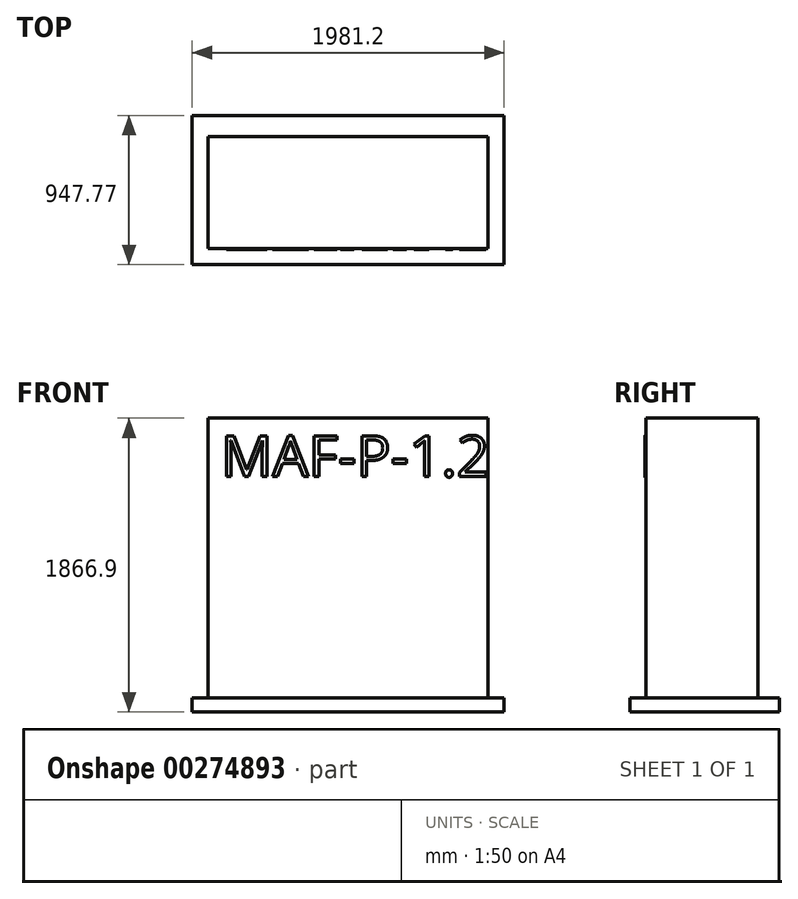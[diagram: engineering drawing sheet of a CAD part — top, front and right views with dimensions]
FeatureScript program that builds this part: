
annotation { "Feature Type Name" : "Feature", "Feature Type Description" : "" }
export const myFeature = defineFeature(function(context is Context, id is Id, definition is map)
    precondition{}
    {
        {
            var Q0;
            Q0=qCreatedBy(makeId("Top.planeOp"),FACE);
            var sketch = newSketch(context, id + "F0", { "sketchPlane" : qUnion([Q0])});
            skLineSegment(sketch, "E0.bottom", {"start": v(0, 0) * mm, "end": v(1778, 0) * mm});
            skLineSegment(sketch, "E0.top", {"start": v(0, 711.2) * mm, "end": v(1778, 711.2) * mm});
            skLineSegment(sketch, "E0.left", {"start": v(0, 0) * mm, "end": v(0, 711.2) * mm});
            skLineSegment(sketch, "E0.right", {"start": v(1778, 0) * mm, "end": v(1778, 711.2) * mm});
            skSolve(sketch);
        }
        {
            var Q0;
            Q0=makeQuery(id+"F0.imprint","IMPRINT",FACE,{"disambiguationData":[TD([[makeQuery(id+"F0.imprint","IMPRINT",EDGE,{"derivedFrom":sQuery(id+"F0.wireOp",EDGE,"E0.bottom")}),1.0]])]});
            extrude(context, id + "F1", {"entities" : qUnion([Q0]), "depth" : 1778 * mm});
        }
        {
            var Q0;
            Q0=makeQuery(id+"F1.opExtrude","SWEPT_FACE",FACE,{"disambiguationData":[OSD([sQuery(id+"F0.wireOp",EDGE,"E0.bottom")])]});
            var sketch = newSketch(context, id + "F2", { "sketchPlane" : qUnion([Q0])});
            skText(sketch, "E1", { "text": "MAF-P-1.2", "fontName": "OpenSans-Regular.ttf"});
            const initialGuessF2  = {"E1": [0.08221, 1.40756, 1, 0, 0.26045]};
            skSetInitialGuess(sketch, initialGuessF2);
            skSolve(sketch);
        }
        {
            var Q0;
            Q0 = qSketchRegion(id + "F2", true);
            extrude(context, id + "F3", {"entities" : qUnion([Q0]), "operationType" : NewBodyOperationType.ADD, "depth" : 6.35 * mm});
        }
        {
            var Q0;
            Q0=makeQuery(id+"F1.opExtrude","CAP_FACE",FACE,{"disambiguationData":[OSD([sQuery(id+"F0.wireOp",EDGE,"E0.bottom"),sQuery(id+"F0.wireOp",EDGE,"E0.top"),sQuery(id+"F0.wireOp",EDGE,"E0.left"),sQuery(id+"F0.wireOp",EDGE,"E0.right")])],"isStart":true});
            extrude(context, id + "F4", {"entities" : qUnion([Q0]), "operationType" : NewBodyOperationType.ADD, "depth" : 88.9 * mm});
        }
        {
            var Q0;
            {var subQ0=sQuery(id+"F0.wireOp",EDGE,"E0.left");Q0=makeQuery(id+"F4.boolean.opBoolean","MERGE",FACE,{"derivedFrom":[makeQuery(id+"F1.opExtrude","SWEPT_FACE",FACE,{"disambiguationData":[OSD([subQ0])]}),makeQuery(id+"F4.opExtrude","SWEPT_FACE",FACE,{"disambiguationData":[OSD([subQ0])]})]});}
            var sketch = newSketch(context, id + "F5", { "sketchPlane" : qUnion([Q0])});
            skLineSegment(sketch, "E2.bottom", {"start": v(-711.2, -88.9) * mm, "end": v(0, -88.9) * mm});
            skLineSegment(sketch, "E2.top", {"start": v(-711.2, 0) * mm, "end": v(0, 0) * mm});
            skLineSegment(sketch, "E2.left", {"start": v(-711.2, -88.9) * mm, "end": v(-711.2, 0) * mm});
            skLineSegment(sketch, "E2.right", {"start": v(0, -88.9) * mm, "end": v(0, 0) * mm});
            skSolve(sketch);
        }
        {
            var Q0;
            Q0=makeQuery(id+"F5.imprint","IMPRINT",FACE,{"disambiguationData":[TD([[makeQuery(id+"F5.imprint","IMPRINT",EDGE,{"derivedFrom":sQuery(id+"F5.wireOp",EDGE,"E2.bottom")}),-1.0]])]});
            extrude(context, id + "F6", {"entities" : qUnion([Q0]), "operationType" : NewBodyOperationType.ADD, "depth" : 101.6 * mm});
        }
        {
            var Q0;
            {var subQ0=sQuery(id+"F0.wireOp",EDGE,"E0.bottom");var subQ1=sQuery(id+"F0.wireOp",EDGE,"E0.left");Q0=makeQuery(id+"F6.boolean.opBoolean","MERGE",FACE,{"derivedFrom":[makeQuery(id+"F4.boolean.opBoolean","MERGE",FACE,{"derivedFrom":[makeQuery(id+"F3.boolean.opBoolean","SPLIT",FACE,{"disambiguationData":[TD([makeQuery(id+"F1.opExtrude","SWEPT_FACE",FACE,{"disambiguationData":[OSD([subQ1])]})])],"derivedFrom":makeQuery(id+"F1.opExtrude","SWEPT_FACE",FACE,{"disambiguationData":[OSD([subQ0])]})}),makeQuery(id+"F4.opExtrude","SWEPT_FACE",FACE,{"disambiguationData":[OSD([subQ0])]})]}),makeQuery(id+"F6.opExtrude","SWEPT_FACE",FACE,{"disambiguationData":[OSD([sQuery(id+"F5.wireOp",EDGE,"E2.right")])]})]});}
            var sketch = newSketch(context, id + "F7", { "sketchPlane" : qUnion([Q0])});
            skLineSegment(sketch, "E3.bottom", {"start": v(-101.6, -88.9) * mm, "end": v(1778, -88.9) * mm});
            skLineSegment(sketch, "E3.top", {"start": v(-101.6, 0) * mm, "end": v(1778, 0) * mm});
            skLineSegment(sketch, "E3.left", {"start": v(-101.6, -88.9) * mm, "end": v(-101.6, 0) * mm});
            skLineSegment(sketch, "E3.right", {"start": v(1778, -88.9) * mm, "end": v(1778, 0) * mm});
            skSolve(sketch);
        }
        {
            var Q0;
            Q0 = qSketchRegion(id + "F7", true);
            extrude(context, id + "F8", {"entities" : qUnion([Q0]), "operationType" : NewBodyOperationType.ADD, "depth" : 101.6 * mm});
        }
        {
            var Q0;
            {var subQ0=sQuery(id+"F0.wireOp",EDGE,"E0.right");Q0=makeQuery(id+"F8.boolean.opBoolean","MERGE",FACE,{"derivedFrom":[makeQuery(id+"F4.boolean.opBoolean","MERGE",FACE,{"derivedFrom":[makeQuery(id+"F1.opExtrude","SWEPT_FACE",FACE,{"disambiguationData":[OSD([subQ0])]}),makeQuery(id+"F4.opExtrude","SWEPT_FACE",FACE,{"disambiguationData":[OSD([subQ0])]})]}),makeQuery(id+"F8.opExtrude","SWEPT_FACE",FACE,{"disambiguationData":[OSD([sQuery(id+"F7.wireOp",EDGE,"E3.right")])]})]});}
            var sketch = newSketch(context, id + "F9", { "sketchPlane" : qUnion([Q0])});
            skLineSegment(sketch, "E4.bottom", {"start": v(-101.6, -88.9) * mm, "end": v(711.2, -88.9) * mm});
            skLineSegment(sketch, "E4.top", {"start": v(-101.6, 0) * mm, "end": v(711.2, 0) * mm});
            skLineSegment(sketch, "E4.left", {"start": v(-101.6, -88.9) * mm, "end": v(-101.6, 0) * mm});
            skLineSegment(sketch, "E4.right", {"start": v(711.2, -88.9) * mm, "end": v(711.2, 0) * mm});
            skSolve(sketch);
        }
        {
            var Q0;
            Q0=makeQuery(id+"F9.imprint","IMPRINT",FACE,{"disambiguationData":[TD([[makeQuery(id+"F9.imprint","IMPRINT",EDGE,{"derivedFrom":sQuery(id+"F9.wireOp",EDGE,"E4.bottom")}),1.0]])]});
            extrude(context, id + "F10", {"entities" : qUnion([Q0]), "operationType" : NewBodyOperationType.ADD, "depth" : 101.6 * mm});
        }
        {
            var Q0;
            {var subQ0=sQuery(id+"F0.wireOp",EDGE,"E0.top");Q0=makeQuery(id+"F10.boolean.opBoolean","MERGE",FACE,{"derivedFrom":[makeQuery(id+"F6.boolean.opBoolean","MERGE",FACE,{"derivedFrom":[makeQuery(id+"F4.boolean.opBoolean","MERGE",FACE,{"derivedFrom":[makeQuery(id+"F1.opExtrude","SWEPT_FACE",FACE,{"disambiguationData":[OSD([subQ0])]}),makeQuery(id+"F4.opExtrude","SWEPT_FACE",FACE,{"disambiguationData":[OSD([subQ0])]})]}),makeQuery(id+"F6.opExtrude","SWEPT_FACE",FACE,{"disambiguationData":[OSD([sQuery(id+"F5.wireOp",EDGE,"E2.left")])]})]}),makeQuery(id+"F10.opExtrude","SWEPT_FACE",FACE,{"disambiguationData":[OSD([sQuery(id+"F9.wireOp",EDGE,"E4.right")])]})]});}
            var sketch = newSketch(context, id + "F11", { "sketchPlane" : qUnion([Q0])});
            skLineSegment(sketch, "E5.bottom", {"start": v(101.6, -88.9) * mm, "end": v(-1879.6, -88.9) * mm});
            skLineSegment(sketch, "E5.top", {"start": v(101.6, 0) * mm, "end": v(-1879.6, 0) * mm});
            skLineSegment(sketch, "E5.left", {"start": v(101.6, -88.9) * mm, "end": v(101.6, 0) * mm});
            skLineSegment(sketch, "E5.right", {"start": v(-1879.6, -88.9) * mm, "end": v(-1879.6, 0) * mm});
            skSolve(sketch);
        }
        {
            var Q0;
            Q0=makeQuery(id+"F11.imprint","IMPRINT",FACE,{"disambiguationData":[TD([[makeQuery(id+"F11.imprint","IMPRINT",EDGE,{"derivedFrom":sQuery(id+"F11.wireOp",EDGE,"E5.bottom")}),-1.0]])]});
            extrude(context, id + "F12", {"entities" : qUnion([Q0]), "operationType" : NewBodyOperationType.ADD, "depth" : 134.97 * mm});
        }
    });
